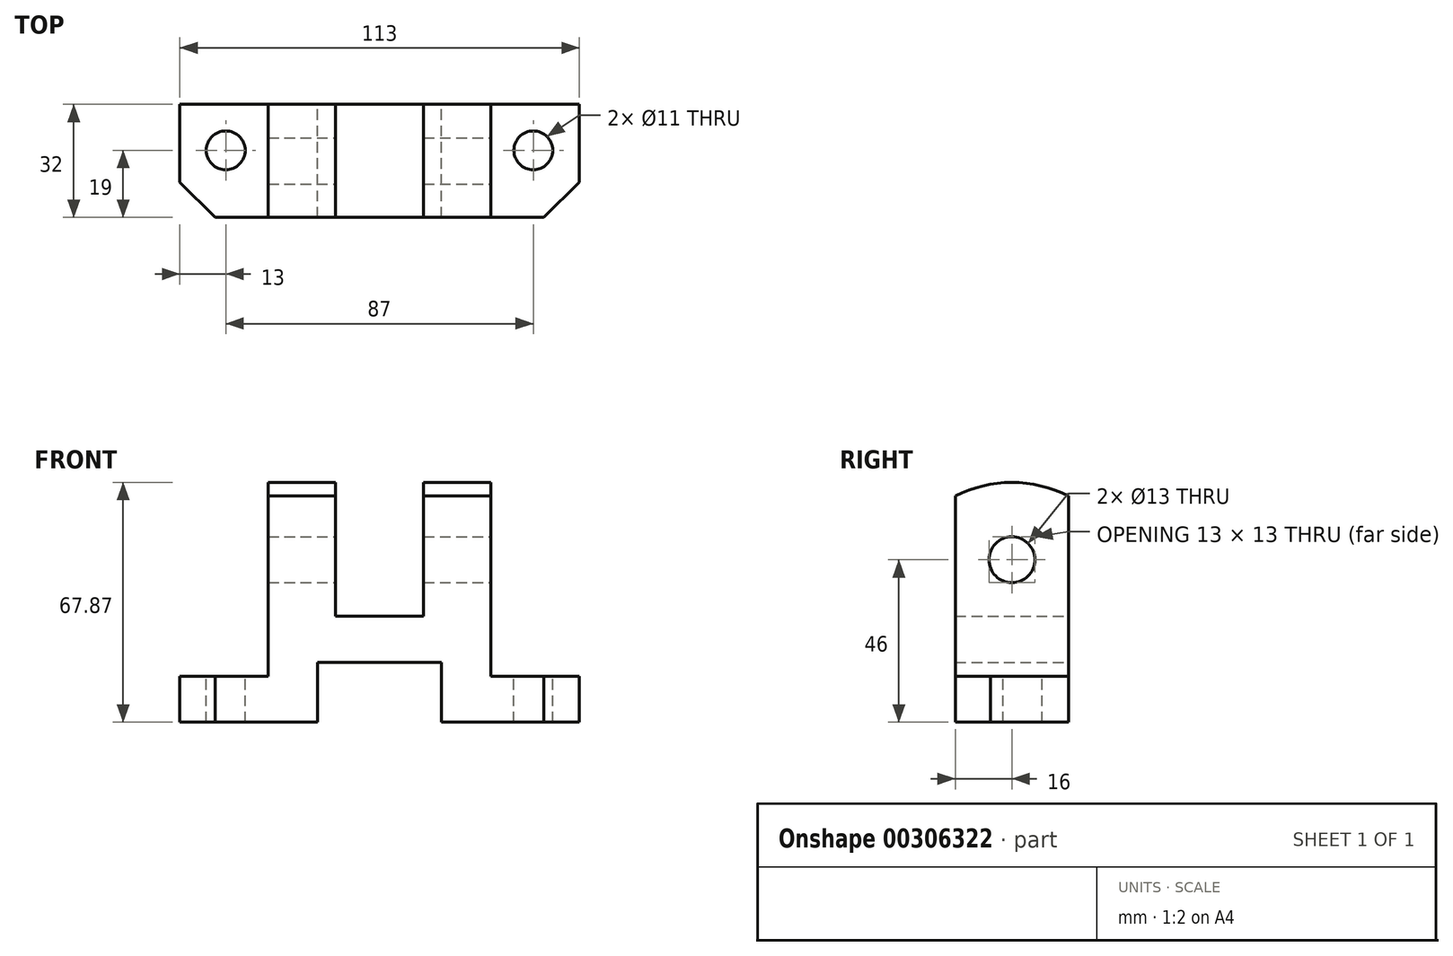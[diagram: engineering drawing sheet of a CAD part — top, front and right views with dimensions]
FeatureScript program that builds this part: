
annotation { "Feature Type Name" : "Feature", "Feature Type Description" : "" }
export const myFeature = defineFeature(function(context is Context, id is Id, definition is map)
    precondition{}
    {
        {
            var Q0;
            Q0=qCreatedBy(makeId("Front.planeOp"),FACE);
            var sketch = newSketch(context, id + "F0", { "sketchPlane" : qUnion([Q0])});
            skLineSegment(sketch, "E0", {"start": v(0, 0) * mm, "end": v(39, 0) * mm});
            skLineSegment(sketch, "E1", {"start": v(0, 0) * mm, "end": v(0, 13) * mm});
            skLineSegment(sketch, "E2", {"start": v(0, 13) * mm, "end": v(25, 13) * mm});
            skLineSegment(sketch, "E3", {"start": v(25, 13) * mm, "end": v(25, 64) * mm});
            skLineSegment(sketch, "E4", {"start": v(25, 64) * mm, "end": v(44, 64) * mm});
            skLineSegment(sketch, "E5", {"start": v(44, 64) * mm, "end": v(44, 30) * mm});
            skLineSegment(sketch, "E6", {"start": v(44, 30) * mm, "end": v(69, 30) * mm});
            skLineSegment(sketch, "E7", {"start": v(69, 30) * mm, "end": v(69, 64) * mm});
            skLineSegment(sketch, "E8", {"start": v(69, 64) * mm, "end": v(88, 64) * mm});
            skLineSegment(sketch, "E9", {"start": v(88, 64) * mm, "end": v(88, 13) * mm});
            skLineSegment(sketch, "E10", {"start": v(88, 13) * mm, "end": v(113, 13) * mm});
            skLineSegment(sketch, "E11", {"start": v(113, 13) * mm, "end": v(113, 0) * mm});
            skLineSegment(sketch, "E12", {"start": v(113, 0) * mm, "end": v(74, 0) * mm});
            skLineSegment(sketch, "E13", {"start": v(74, 0) * mm, "end": v(74, 17) * mm});
            skLineSegment(sketch, "E14", {"start": v(39, 0) * mm, "end": v(39, 17) * mm});
            skLineSegment(sketch, "E15", {"start": v(39, 17) * mm, "end": v(74, 17) * mm});
            skSolve(sketch);
        }
        {
            var Q0;
            Q0 = qSketchRegion(id + "F0", true);
            extrude(context, id + "F1", {"entities" : qUnion([Q0]), "depth" : 32 * mm});
        }
        {
            var Q0;
            Q0=makeQuery(id+"F1.opExtrude","SWEPT_FACE",FACE,{"disambiguationData":[OSD([sQuery(id+"F0.wireOp",EDGE,"E10")])]});
            var sketch = newSketch(context, id + "F2", { "sketchPlane" : qUnion([Q0])});
            skCircle(sketch, "E16", {"center": v(100, -13) * mm, "radius": 5.5 * mm});
            skSolve(sketch);
        }
        {
            var Q0;
            Q0 = qSketchRegion(id + "F2", true);
            extrude(context, id + "F3", {"entities" : qUnion([Q0]), "operationType" : NewBodyOperationType.REMOVE, "endBound" : BoundingType.THROUGH_ALL, "oppositeDirection" : true, "depth" : 25 * mm});
        }
        {
            var Q0;
            Q0=makeQuery(id+"F1.opExtrude","SWEPT_FACE",FACE,{"disambiguationData":[OSD([sQuery(id+"F0.wireOp",EDGE,"E2")])]});
            var sketch = newSketch(context, id + "F4", { "sketchPlane" : qUnion([Q0])});
            skCircle(sketch, "E17", {"center": v(13, -13) * mm, "radius": 5.5 * mm});
            skSolve(sketch);
        }
        {
            var Q0;
            Q0 = qSketchRegion(id + "F4", true);
            extrude(context, id + "F5", {"entities" : qUnion([Q0]), "operationType" : NewBodyOperationType.REMOVE, "endBound" : BoundingType.THROUGH_ALL, "oppositeDirection" : true, "depth" : 25 * mm});
        }
        {
            var Q0;
            Q0=makeQuery(id+"F1.opExtrude","SWEPT_FACE",FACE,{"disambiguationData":[OSD([sQuery(id+"F0.wireOp",EDGE,"E9")])]});
            var sketch = newSketch(context, id + "F6", { "sketchPlane" : qUnion([Q0])});
            skCircle(sketch, "E18", {"center": v(-16, 46) * mm, "radius": 6.5 * mm});
            skSolve(sketch);
        }
        {
            var Q0;
            Q0 = qSketchRegion(id + "F6", true);
            extrude(context, id + "F7", {"entities" : qUnion([Q0]), "operationType" : NewBodyOperationType.REMOVE, "endBound" : BoundingType.THROUGH_ALL, "oppositeDirection" : true, "depth" : 25 * mm});
        }
        {
            var Q0;
            Q0=makeQuery(id+"F1.opExtrude","SWEPT_FACE",FACE,{"disambiguationData":[OSD([sQuery(id+"F0.wireOp",EDGE,"E10")])]});
            var sketch = newSketch(context, id + "F8", { "sketchPlane" : qUnion([Q0])});
            skLineSegment(sketch, "E19", {"start": v(113, -32) * mm, "end": v(103, -32) * mm});
            skLineSegment(sketch, "E20", {"start": v(103, -32) * mm, "end": v(113, -22) * mm});
            skLineSegment(sketch, "E21", {"start": v(113, -22) * mm, "end": v(113, -32) * mm});
            skSolve(sketch);
        }
        {
            var Q0;
            Q0 = qSketchRegion(id + "F8", true);
            extrude(context, id + "F9", {"entities" : qUnion([Q0]), "operationType" : NewBodyOperationType.REMOVE, "endBound" : BoundingType.THROUGH_ALL, "oppositeDirection" : true, "depth" : 25 * mm});
        }
        {
            var Q0;
            Q0=makeQuery(id+"F1.opExtrude","SWEPT_FACE",FACE,{"disambiguationData":[OSD([sQuery(id+"F0.wireOp",EDGE,"E2")])]});
            var sketch = newSketch(context, id + "F10", { "sketchPlane" : qUnion([Q0])});
            skLineSegment(sketch, "E22", {"start": v(0, -22) * mm, "end": v(0, -32) * mm});
            skLineSegment(sketch, "E23", {"start": v(0, -32) * mm, "end": v(10, -32) * mm});
            skLineSegment(sketch, "E24", {"start": v(10, -32) * mm, "end": v(0, -22) * mm});
            skSolve(sketch);
        }
        {
            var Q0;
            Q0 = qSketchRegion(id + "F10", true);
            extrude(context, id + "F11", {"entities" : qUnion([Q0]), "operationType" : NewBodyOperationType.REMOVE, "endBound" : BoundingType.THROUGH_ALL, "oppositeDirection" : true, "depth" : 25 * mm});
        }
        {
            var Q0;
            Q0=makeQuery(id+"F1.opExtrude","SWEPT_FACE",FACE,{"disambiguationData":[OSD([sQuery(id+"F0.wireOp",EDGE,"E9")])]});
            var sketch = newSketch(context, id + "F12", { "sketchPlane" : qUnion([Q0])});
            skSolve(sketch);
        }
        {
            var Q0;
            {var subQ0=sQuery(id+"F0.wireOp",EDGE,"E9");Q0=makeQuery(id+"F12.imprint","IMPRINT",FACE,{"disambiguationData":[TD([[makeQuery(id+"F12.imprint","IMPRINT",EDGE,{"derivedFrom":makeQuery(id+"F1.opExtrude","CAP_EDGE",EDGE,{"disambiguationData":[OSD([subQ0])],"isStart":true})}),-1.0]])]});}
            var sketch = newSketch(context, id + "F13", { "sketchPlane" : qUnion([Q0])});
            skArc(sketch, "E25", {"start": v(0, 64) * mm, "mid": v(-16, 67.87) * mm, "end": v(-32, 64) * mm});
            skLineSegment(sketch, "E26", {"start": v(-32, 64) * mm, "end": v(0, 64) * mm});
            skSolve(sketch);
        }
        {
            var Q0;
            Q0 = qSketchRegion(id + "F13", true);
            extrude(context, id + "F14", {"entities" : qUnion([Q0]), "oppositeDirection" : true, "depth" : 63 * mm});
        }
        {
            var Q0;
            Q0=makeQuery(id+"F14.opExtrude","SWEPT_BODY",BODY,{"disambiguationData":[OSD([sQuery(id+"F13.wireOp",EDGE,"E25"),sQuery(id+"F13.wireOp",EDGE,"E26")])]});
            deleteBodies(context, id + "F15", {"entities" : qUnion([Q0])});
        }
        {
            var Q0;
            {var subQ0=sQuery(id+"F0.wireOp",EDGE,"E9");Q0=makeQuery(id+"F12.imprint","IMPRINT",FACE,{"disambiguationData":[TD([[makeQuery(id+"F12.imprint","IMPRINT",EDGE,{"derivedFrom":makeQuery(id+"F1.opExtrude","CAP_EDGE",EDGE,{"disambiguationData":[OSD([subQ0])],"isStart":true})}),-1.0]])]});}
            var sketch = newSketch(context, id + "F16", { "sketchPlane" : qUnion([Q0])});
            skArc(sketch, "E27", {"start": v(0, 64) * mm, "mid": v(-16, 67.87) * mm, "end": v(-32, 64) * mm});
            skLineSegment(sketch, "E28", {"start": v(-32, 64) * mm, "end": v(0, 64) * mm});
            skSolve(sketch);
        }
        {
            var Q0;
            Q0 = qSketchRegion(id + "F16", true);
            extrude(context, id + "F17", {"entities" : qUnion([Q0]), "operationType" : NewBodyOperationType.ADD, "oppositeDirection" : true, "depth" : 63 * mm});
        }
        {
            var Q0;
            Q0=qCreatedBy(makeId("Front.planeOp"),FACE);
            var sketch = newSketch(context, id + "F18", { "sketchPlane" : qUnion([Q0])});
            skLineSegment(sketch, "E29.bottom", {"start": v(44, 64) * mm, "end": v(69, 64) * mm});
            skLineSegment(sketch, "E29.top", {"start": v(44, 68.46) * mm, "end": v(69, 68.46) * mm});
            skLineSegment(sketch, "E29.left", {"start": v(44, 64) * mm, "end": v(44, 68.46) * mm});
            skLineSegment(sketch, "E29.right", {"start": v(69, 64) * mm, "end": v(69, 68.46) * mm});
            skSolve(sketch);
        }
        {
            var Q0;
            Q0 = qSketchRegion(id + "F18", true);
            extrude(context, id + "F19", {"entities" : qUnion([Q0]), "operationType" : NewBodyOperationType.REMOVE, "endBound" : BoundingType.THROUGH_ALL, "depth" : 25 * mm});
        }
    });
